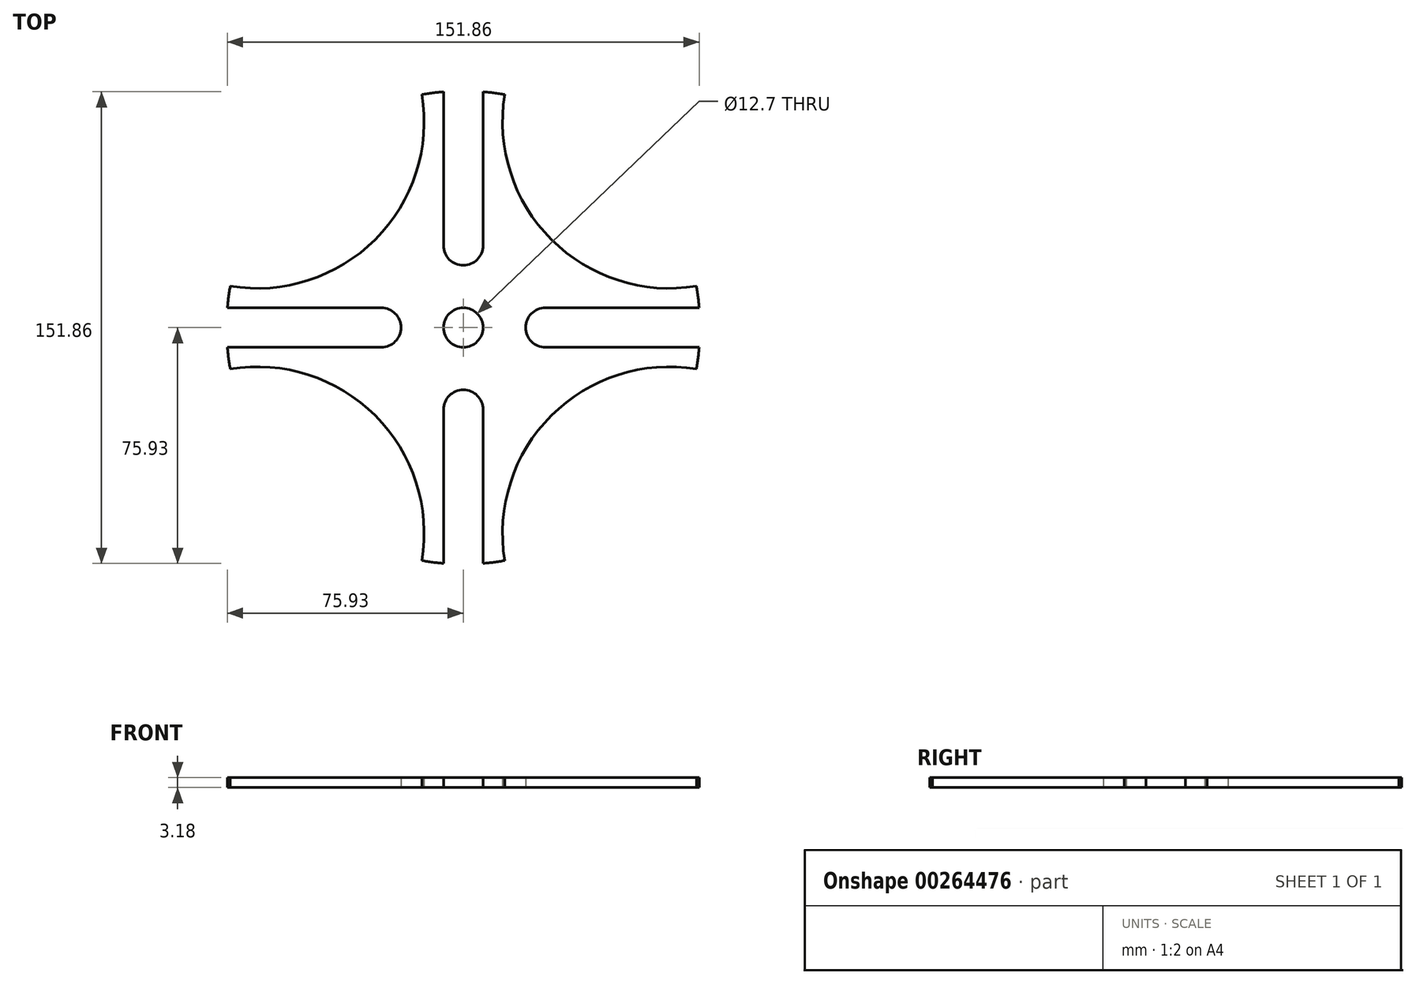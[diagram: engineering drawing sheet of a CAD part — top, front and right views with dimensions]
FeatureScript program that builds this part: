
annotation { "Feature Type Name" : "Feature", "Feature Type Description" : "" }
export const myFeature = defineFeature(function(context is Context, id is Id, definition is map)
    precondition{}
    {
        {
            var Q0;
            Q0=qCreatedBy(makeId("Top.planeOp"),FACE);
            var sketch = newSketch(context, id + "F0", { "sketchPlane" : qUnion([Q0])});
            skArc(sketch, "E0", {"start": v(-6.35, 75.93) * mm, "mid": v(-9.85, 75.56) * mm, "end": v(-13.34, 75.02) * mm});
            skPoint(sketch, "E1.start.orphan", {"position": v(6.35, 42.86) * mm});
            skLineSegment(sketch, "E2", {"start": v(6.35, 42.86) * mm, "end": v(6.35, 75.93) * mm});
            skLineSegment(sketch, "E3", {"start": v(-6.35, 42.86) * mm, "end": v(-6.35, 75.93) * mm});
            skLineSegment(sketch, "E4.MirrorCS", {"start": v(-6.35, -42.86) * mm, "end": v(-6.35, -75.93) * mm});
            skLineSegment(sketch, "E5.MirrorCS", {"start": v(6.35, -42.86) * mm, "end": v(6.35, -75.93) * mm});
            skLineSegment(sketch, "E6.MirrorCS", {"start": v(-42.86, -6.35) * mm, "end": v(-75.93, -6.35) * mm});
            skLineSegment(sketch, "E7.MirrorCS", {"start": v(-42.86, 6.35) * mm, "end": v(-75.93, 6.35) * mm});
            skLineSegment(sketch, "E8.MirrorCS", {"start": v(42.86, -6.35) * mm, "end": v(75.93, -6.35) * mm});
            skLineSegment(sketch, "E9.MirrorCS", {"start": v(42.86, 6.35) * mm, "end": v(75.93, 6.35) * mm});
            skArc(sketch, "E10.trimOffspring", {"start": v(-75.93, -6.35) * mm, "mid": v(-75.56, -9.85) * mm, "end": v(-75.02, -13.34) * mm});
            skArc(sketch, "E11.trimOffspring", {"start": v(6.35, -75.93) * mm, "mid": v(9.85, -75.56) * mm, "end": v(13.34, -75.02) * mm});
            skArc(sketch, "E12", {"start": v(-75.02, 13.33) * mm, "mid": v(-28.35, 28.35) * mm, "end": v(-13.34, 75.02) * mm});
            skArc(sketch, "E13.MirrorCS", {"start": v(75.02, 13.33) * mm, "mid": v(28.35, 28.35) * mm, "end": v(13.34, 75.02) * mm});
            skArc(sketch, "E14.MirrorCS", {"start": v(-75.02, -13.34) * mm, "mid": v(-28.35, -28.35) * mm, "end": v(-13.33, -75.02) * mm});
            skArc(sketch, "E15.MirrorCS", {"start": v(75.02, -13.33) * mm, "mid": v(28.35, -28.35) * mm, "end": v(13.34, -75.02) * mm});
            skArc(sketch, "E16.trimOffspring", {"start": v(-75.02, 13.33) * mm, "mid": v(-75.56, 9.85) * mm, "end": v(-75.93, 6.35) * mm});
            skArc(sketch, "E17.trimOffspring", {"start": v(13.34, 75.02) * mm, "mid": v(9.85, 75.56) * mm, "end": v(6.35, 75.93) * mm});
            skArc(sketch, "E18.trimOffspring", {"start": v(75.02, -13.33) * mm, "mid": v(75.56, -9.85) * mm, "end": v(75.93, -6.35) * mm});
            skArc(sketch, "E19.trimOffspring", {"start": v(-13.33, -75.02) * mm, "mid": v(-9.85, -75.56) * mm, "end": v(-6.35, -75.93) * mm});
            skCircle(sketch, "E20", {"center": v(0, 0) * mm, "radius": 6.35 * mm});
            skPoint(sketch, "E21", {"position": v(-8.76, 0) * mm});
            skPoint(sketch, "E22.MirrorCS.center.orphan", {"position": v(-26.4, 0) * mm});
            skLineSegment(sketch, "E23", {"start": v(-42.86, 6.35) * mm, "end": v(-26.4, 6.35) * mm});
            skLineSegment(sketch, "E24", {"start": v(-42.86, -6.35) * mm, "end": v(-26.4, -6.35) * mm});
            skArc(sketch, "E25", {"start": v(-26.4, -6.35) * mm, "mid": v(-20.05, 0) * mm, "end": v(-26.4, 6.35) * mm});
            skArc(sketch, "E26.MirrorCS", {"start": v(75.93, -6.35) * mm, "mid": v(75.56, -9.85) * mm, "end": v(75.02, -13.34) * mm});
            skArc(sketch, "E27.MirrorCS", {"start": v(13.33, -75.02) * mm, "mid": v(9.85, -75.56) * mm, "end": v(6.35, -75.93) * mm});
            skArc(sketch, "E28.MirrorCS", {"start": v(75.02, 13.33) * mm, "mid": v(75.56, 9.85) * mm, "end": v(75.93, 6.35) * mm});
            skPoint(sketch, "E29.MirrorP", {"position": v(26.4, 0) * mm});
            skLineSegment(sketch, "E30.MirrorCS", {"start": v(42.86, -6.35) * mm, "end": v(26.4, -6.35) * mm});
            skLineSegment(sketch, "E31.MirrorCS", {"start": v(42.86, 6.35) * mm, "end": v(26.4, 6.35) * mm});
            skArc(sketch, "E32.MirrorCS", {"start": v(26.4, -6.35) * mm, "mid": v(20.05, 0) * mm, "end": v(26.4, 6.35) * mm});
            skArc(sketch, "E33.MirrorCS", {"start": v(75.02, -13.34) * mm, "mid": v(28.35, -28.35) * mm, "end": v(13.33, -75.02) * mm});
            skPoint(sketch, "E34.MirrorP", {"position": v(8.76, 0) * mm});
            skArc(sketch, "E35.MirrorCS", {"start": v(-13.33, -75.02) * mm, "mid": v(-28.35, -28.35) * mm, "end": v(-75.02, -13.34) * mm});
            skArc(sketch, "E36.MirrorCS", {"start": v(-6.35, -26.4) * mm, "mid": v(0, -20.05) * mm, "end": v(6.35, -26.4) * mm});
            skLineSegment(sketch, "E37.MirrorCS", {"start": v(6.35, -42.86) * mm, "end": v(6.35, -26.4) * mm});
            skArc(sketch, "E38.MirrorCS", {"start": v(13.33, -75.02) * mm, "mid": v(28.35, -28.35) * mm, "end": v(75.02, -13.34) * mm});
            skLineSegment(sketch, "E39.MirrorCS", {"start": v(6.35, 42.86) * mm, "end": v(6.35, 26.4) * mm});
            skArc(sketch, "E40.MirrorCS", {"start": v(-6.35, 26.4) * mm, "mid": v(0, 20.05) * mm, "end": v(6.35, 26.4) * mm});
            skLineSegment(sketch, "E41.MirrorCS", {"start": v(-6.35, 42.86) * mm, "end": v(-6.35, 26.4) * mm});
            skPoint(sketch, "E42.MirrorCS.end.orphan", {"position": v(-6.35, -26.4) * mm});
            skPoint(sketch, "E42.MirrorCS.start.orphan", {"position": v(-6.35, -42.86) * mm});
            skLineSegment(sketch, "E43", {"start": v(-6.35, -26.4) * mm, "end": v(-6.35, -42.86) * mm});
            skPoint(sketch, "E44.trimOffspring.center.orphan", {"position": v(27.75, 0) * mm});
            skLineSegment(sketch, "E45", {"start": v(-75.93, 6.35) * mm, "end": v(-75.93, -6.35) * mm});
            skSolve(sketch);
        }
        {
            var Q0;
            Q0=makeQuery(id+"F0.imprint","IMPRINT",FACE,{"disambiguationData":[TD([[makeQuery(id+"F0.imprint","IMPRINT",EDGE,{"derivedFrom":sQuery(id+"F0.wireOp",EDGE,"E0")}),1.0]])]});
            extrude(context, id + "F1", {"entities" : qUnion([Q0]), "depth" : 3.17 * mm});
        }
    });
